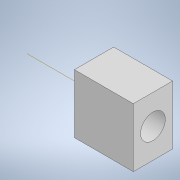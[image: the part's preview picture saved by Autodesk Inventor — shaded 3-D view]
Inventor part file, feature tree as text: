
AUTODESK INVENTOR PART (.ipt)
format: ipt  version: 2022 (Build 260153000, 153)  size: 116,224 bytes
history: native  units: mm
features: sketch x4, extrude x2, other x1, hole x1
ambient origin geometry x8: Origin, YZ Plane, XZ Plane, XY Plane, X Axis, Y Axis, Z Axis, Center Point
bodies: Solid1 (feature_tree)
feature tree (8):
  extrude  "Extrusion1"  Depth=9.525mm
  sketch  "Sketch2"  dims[d2=1.0mm d3=6.35mm d4=0.0mm]
  other  "Work Axis1"
  extrude  "Extrusion2"  Depth=6.35mm TaperAngle=0.0deg
  hole  "Hole1"  [1 undecoded]
  sketch  "Sketch1"  dims[d0=9.525mm d1=9.525mm]
  sketch  "Sketch3"  dims[d5=4.0mm d6=6.0mm d7=4.0mm d8=2.0mm d9=90.0deg d10=8.0mm d11=20.594885mm d12=10.0mm d13=0.0mm]
  sketch  "Sketch4"
note: 1 required parameter value undecoded (feature->parameter linkage not recoverable at this tier; creation-order binding heuristic only, values carry confidence <= 0.55)
